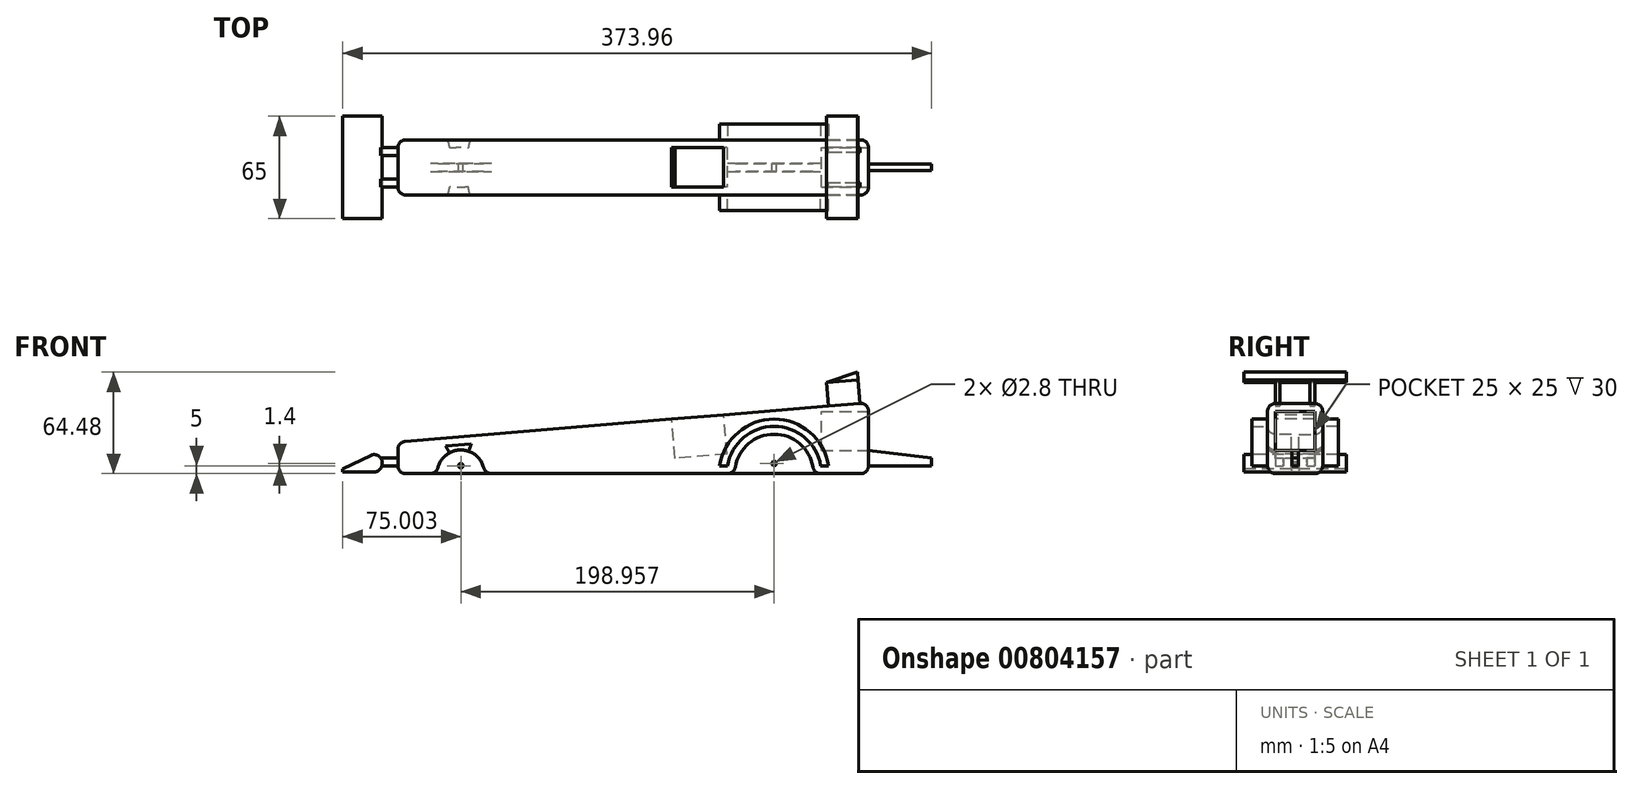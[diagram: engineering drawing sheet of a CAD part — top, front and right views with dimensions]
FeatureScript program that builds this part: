
annotation { "Feature Type Name" : "Feature", "Feature Type Description" : "" }
export const myFeature = defineFeature(function(context is Context, id is Id, definition is map)
    precondition{}
    {
        {
            var Q0;
            Q0=qCreatedBy(makeId("Front.planeOp"),FACE);
            var sketch = newSketch(context, id + "F0", { "sketchPlane" : qUnion([Q0])});
            skLineSegment(sketch, "E0", {"start": v(0, 0) * mm, "end": v(-298.96, -25) * mm});
            skLineSegment(sketch, "E1", {"start": v(-298.96, -25) * mm, "end": v(-298.96, -45) * mm});
            skLineSegment(sketch, "E2", {"start": v(-298.96, -45) * mm, "end": v(0, -45) * mm});
            skLineSegment(sketch, "E3", {"start": v(0, -45) * mm, "end": v(0, 0) * mm});
            skSolve(sketch);
        }
        {
            var Q0;
            Q0 = qSketchRegion(id + "F0", true);
            extrude(context, id + "F1", {"entities" : qUnion([Q0]), "depth" : 35 * mm, "offsetDistance" : 25 * mm});
        }
        {
            var Q0;
            Q0=makeQuery(id+"F1.opExtrude","CAP_FACE",FACE,{"disambiguationData":[OSD([sQuery(id+"F0.wireOp",EDGE,"E0"),sQuery(id+"F0.wireOp",EDGE,"E1"),sQuery(id+"F0.wireOp",EDGE,"E2"),sQuery(id+"F0.wireOp",EDGE,"E3")])],"isStart":false});
            var sketch = newSketch(context, id + "F2", { "sketchPlane" : qUnion([Q0])});
            skCircle(sketch, "E4", {"center": v(-258.96, -45) * mm, "radius": 15 * mm});
            skSolve(sketch);
        }
        {
            var Q0;
            Q0 = qSketchRegion(id + "F2", true);
            var Q1;
            Q1=makeQuery(id+"F1.opExtrude","CAP_FACE",FACE,{"disambiguationData":[OSD([sQuery(id+"F0.wireOp",EDGE,"E0"),sQuery(id+"F0.wireOp",EDGE,"E1"),sQuery(id+"F0.wireOp",EDGE,"E2"),sQuery(id+"F0.wireOp",EDGE,"E3")])],"isStart":true});
            extrude(context, id + "F3", {"entities" : qUnion([Q0, Q1]), "operationType" : NewBodyOperationType.REMOVE, "oppositeDirection" : true, "depth" : 15 * mm, "offsetDistance" : 25 * mm});
        }
        {
            var Q0;
            Q0=makeQuery(id+"F1.opExtrude","CAP_FACE",FACE,{"disambiguationData":[OSD([sQuery(id+"F0.wireOp",EDGE,"E0"),sQuery(id+"F0.wireOp",EDGE,"E1"),sQuery(id+"F0.wireOp",EDGE,"E2"),sQuery(id+"F0.wireOp",EDGE,"E3")])],"isStart":true});
            var sketch = newSketch(context, id + "F4", { "sketchPlane" : qUnion([Q0])});
            skCircle(sketch, "E5", {"center": v(258.96, -45) * mm, "radius": 15 * mm});
            skSolve(sketch);
        }
        {
            var Q0;
            Q0 = qSketchRegion(id + "F4", true);
            extrude(context, id + "F5", {"entities" : qUnion([Q0]), "operationType" : NewBodyOperationType.REMOVE, "oppositeDirection" : true, "depth" : 15 * mm, "offsetDistance" : 25 * mm});
        }
        {
            var Q0;
            Q0=makeQuery(id+"F5.boolean.opBoolean","COPY",FACE,{"derivedFrom":makeQuery(id+"F5.opExtrude","CAP_FACE",FACE,{"disambiguationData":[OSD([sQuery(id+"F4.wireOp",EDGE,"E5")])],"isStart":false})});
            var sketch = newSketch(context, id + "F6", { "sketchPlane" : qUnion([Q0])});
            skCircle(sketch, "E6", {"center": v(258.96, -40) * mm, "radius": 1.4 * mm});
            skPoint(sketch, "E6.centerSnap0", {"position": v(258.96, -45) * mm});
            skSolve(sketch);
        }
        {
            var Q0;
            Q0 = qSketchRegion(id + "F6", true);
            extrude(context, id + "F7", {"entities" : qUnion([Q0]), "operationType" : NewBodyOperationType.REMOVE, "oppositeDirection" : true, "depth" : 25 * mm, "offsetDistance" : 25 * mm});
        }
        {
            var Q0;
            Q0=makeQuery(id+"F1.opExtrude","CAP_FACE",FACE,{"disambiguationData":[OSD([sQuery(id+"F0.wireOp",EDGE,"E0"),sQuery(id+"F0.wireOp",EDGE,"E1"),sQuery(id+"F0.wireOp",EDGE,"E2"),sQuery(id+"F0.wireOp",EDGE,"E3")])],"isStart":false});
            var sketch = newSketch(context, id + "F8", { "sketchPlane" : qUnion([Q0])});
            skCircle(sketch, "E7", {"center": v(-60, -45) * mm, "radius": 25 * mm});
            skSolve(sketch);
        }
        {
            var Q0;
            Q0 = qSketchRegion(id + "F8", true);
            extrude(context, id + "F9", {"entities" : qUnion([Q0]), "operationType" : NewBodyOperationType.REMOVE, "oppositeDirection" : true, "depth" : 15 * mm, "offsetDistance" : 25 * mm});
        }
        {
            var Q0;
            Q0=makeQuery(id+"F1.opExtrude","CAP_FACE",FACE,{"disambiguationData":[OSD([sQuery(id+"F0.wireOp",EDGE,"E0"),sQuery(id+"F0.wireOp",EDGE,"E1"),sQuery(id+"F0.wireOp",EDGE,"E2"),sQuery(id+"F0.wireOp",EDGE,"E3")])],"isStart":true});
            var sketch = newSketch(context, id + "F10", { "sketchPlane" : qUnion([Q0])});
            skCircle(sketch, "E8", {"center": v(60, -45) * mm, "radius": 25 * mm});
            skSolve(sketch);
        }
        {
            var Q0;
            Q0 = qSketchRegion(id + "F10", true);
            extrude(context, id + "F11", {"entities" : qUnion([Q0]), "operationType" : NewBodyOperationType.REMOVE, "oppositeDirection" : true, "depth" : 15 * mm, "offsetDistance" : 25 * mm});
        }
        {
            var Q0;
            Q0=makeQuery(id+"F11.boolean.opBoolean","COPY",FACE,{"derivedFrom":makeQuery(id+"F11.opExtrude","CAP_FACE",FACE,{"disambiguationData":[OSD([sQuery(id+"F10.wireOp",EDGE,"E8")])],"isStart":false})});
            var sketch = newSketch(context, id + "F12", { "sketchPlane" : qUnion([Q0])});
            skCircle(sketch, "E9", {"center": v(60, -38.6) * mm, "radius": 1.4 * mm});
            skPoint(sketch, "E9.centerSnap0", {"position": v(60, -45) * mm});
            skSolve(sketch);
        }
        {
            var Q0;
            Q0=makeQuery(id+"F12.imprint","IMPRINT",FACE,{"disambiguationData":[TD([[makeQuery(id+"F12.imprint","IMPRINT",EDGE,{"derivedFrom":sQuery(id+"F12.wireOp",EDGE,"E9")}),1.0]])]});
            extrude(context, id + "F13", {"entities" : qUnion([Q0]), "operationType" : NewBodyOperationType.REMOVE, "oppositeDirection" : true, "depth" : 25 * mm, "offsetDistance" : 25 * mm});
        }
        {
            var Q0;
            Q0=makeQuery(id+"F1.opExtrude","CAP_EDGE",EDGE,{"disambiguationData":[OSD([sQuery(id+"F0.wireOp",EDGE,"E0")])],"isStart":true});
            fillet(context, id + "F14", {"entities" : qUnion([Q0]), "radius" : 5 * mm, "tangentPropagation" : true, "allowEdgeOverflow" : false});
        }
        {
            var Q0;
            Q0=makeQuery(id+"F1.opExtrude","CAP_EDGE",EDGE,{"disambiguationData":[OSD([sQuery(id+"F0.wireOp",EDGE,"E0")])],"isStart":false});
            fillet(context, id + "F15", {"entities" : qUnion([Q0]), "radius" : 5 * mm, "tangentPropagation" : true, "allowEdgeOverflow" : false});
        }
        {
            var Q0;
            Q0=makeQuery(id+"F1.opExtrude","SWEPT_EDGE",EDGE,{"disambiguationData":[OSD([sQuery(id+"F0.wireOp",EDGE,"E0"),sQuery(id+"F0.wireOp",EDGE,"E1")])]});
            fillet(context, id + "F16", {"entities" : qUnion([Q0]), "radius" : 5 * mm, "tangentPropagation" : true, "allowEdgeOverflow" : false});
        }
        {
            var Q0;
            Q0=makeQuery(id+"F1.opExtrude","SWEPT_EDGE",EDGE,{"disambiguationData":[OSD([sQuery(id+"F0.wireOp",EDGE,"E0"),sQuery(id+"F0.wireOp",EDGE,"E3")])]});
            fillet(context, id + "F17", {"entities" : qUnion([Q0]), "radius" : 5 * mm, "tangentPropagation" : true, "allowEdgeOverflow" : false});
        }
        {
            var Q0;
            {var subQ0=sQuery(id+"F0.wireOp",EDGE,"E3");var subQ1=sQuery(id+"F0.wireOp",EDGE,"E2");var subQ4=makeQuery(id+"F3.opExtrude","SWEPT_FACE",FACE,{"disambiguationData":[OSD([sQuery(id+"F2.wireOp",EDGE,"E4")])]});Q0=makeQuery(id+"F9.boolean.opBoolean","SPLIT",EDGE,{"disambiguationData":[TD([makeQuery(id+"F3.boolean.opBoolean","COPY",FACE,{"derivedFrom":subQ4})])],"derivedFrom":makeQuery(id+"F3.boolean.opBoolean","SPLIT",EDGE,{"disambiguationData":[TD([makeQuery(id+"F1.opExtrude","SWEPT_FACE",FACE,{"disambiguationData":[OSD([subQ0])]})])],"derivedFrom":makeQuery(id+"F1.opExtrude","CAP_EDGE",EDGE,{"disambiguationData":[OSD([subQ1])],"isStart":false})})});}
            var Q1;
            Q1=makeQuery(id+"F1.opExtrude","CAP_FACE",FACE,{"disambiguationData":[OSD([sQuery(id+"F0.wireOp",EDGE,"E0"),sQuery(id+"F0.wireOp",EDGE,"E1"),sQuery(id+"F0.wireOp",EDGE,"E2"),sQuery(id+"F0.wireOp",EDGE,"E3")])],"isStart":false});
            fillet(context, id + "F18", {"entities" : qUnion([Q0, Q1]), "radius" : 5 * mm, "tangentPropagation" : true, "allowEdgeOverflow" : false});
        }
        {
            var Q0;
            Q0=makeQuery(id+"F1.opExtrude","CAP_FACE",FACE,{"disambiguationData":[OSD([sQuery(id+"F0.wireOp",EDGE,"E0"),sQuery(id+"F0.wireOp",EDGE,"E1"),sQuery(id+"F0.wireOp",EDGE,"E2"),sQuery(id+"F0.wireOp",EDGE,"E3")])],"isStart":true});
            fillet(context, id + "F19", {"entities" : qUnion([Q0]), "radius" : 5 * mm, "tangentPropagation" : true, "allowEdgeOverflow" : false});
        }
        {
            var Q0;
            Q0=makeQuery(id+"F1.opExtrude","SWEPT_FACE",FACE,{"disambiguationData":[OSD([sQuery(id+"F0.wireOp",EDGE,"E0")])]});
            var sketch = newSketch(context, id + "F20", { "sketchPlane" : qUnion([Q0])});
            skLineSegment(sketch, "E10", {"start": v(-5.44, -5) * mm, "end": v(-25.44, -5) * mm});
            skLineSegment(sketch, "E11", {"start": v(-5.44, -30) * mm, "end": v(-25.44, -30) * mm});
            skLineSegment(sketch, "E12", {"start": v(-5.44, -5) * mm, "end": v(-5.44, -8) * mm});
            skLineSegment(sketch, "E13", {"start": v(-5.44, -8) * mm, "end": v(-25.44, -8) * mm});
            skLineSegment(sketch, "E14", {"start": v(-25.44, -8) * mm, "end": v(-25.44, -5) * mm});
            skLineSegment(sketch, "E15", {"start": v(-25.44, -30) * mm, "end": v(-25.44, -27) * mm});
            skLineSegment(sketch, "E16", {"start": v(-25.44, -27) * mm, "end": v(-5.44, -27) * mm});
            skLineSegment(sketch, "E17", {"start": v(-5.44, -27) * mm, "end": v(-5.44, -30) * mm});
            skSolve(sketch);
        }
        {
            var Q0;
            Q0 = qSketchRegion(id + "F20", true);
            extrude(context, id + "F21", {"entities" : qUnion([Q0]), "operationType" : NewBodyOperationType.ADD, "depth" : 15 * mm, "offsetDistance" : 25 * mm});
        }
        {
            var Q0;
            Q0=makeQuery(id+"F21.opExtrude","CAP_FACE",FACE,{"disambiguationData":[OSD([sQuery(id+"F20.wireOp",EDGE,"E10"),sQuery(id+"F20.wireOp",EDGE,"E12"),sQuery(id+"F20.wireOp",EDGE,"E13"),sQuery(id+"F20.wireOp",EDGE,"E14")])],"isStart":false});
            var sketch = newSketch(context, id + "F22", { "sketchPlane" : qUnion([Q0])});
            skLineSegment(sketch, "E18", {"start": v(-25.44, -5) * mm, "end": v(-25.44, -29.95) * mm});
            skLineSegment(sketch, "E19", {"start": v(-5.53, -29.95) * mm, "end": v(-5.44, -5) * mm});
            skLineSegment(sketch, "E20", {"start": v(-25.44, -5) * mm, "end": v(-25.44, 15) * mm});
            skLineSegment(sketch, "E21", {"start": v(-25.44, 15) * mm, "end": v(-5.44, 15) * mm});
            skLineSegment(sketch, "E22", {"start": v(-5.44, 15) * mm, "end": v(-5.44, -5) * mm});
            skLineSegment(sketch, "E23", {"start": v(-25.44, -29.95) * mm, "end": v(-25.44, -49.95) * mm});
            skLineSegment(sketch, "E24", {"start": v(-25.44, -49.95) * mm, "end": v(-5.53, -49.95) * mm});
            skLineSegment(sketch, "E25", {"start": v(-5.53, -49.95) * mm, "end": v(-5.53, -29.95) * mm});
            skSolve(sketch);
        }
        {
            var Q0;
            Q0 = qSketchRegion(id + "F22", true);
            extrude(context, id + "F23", {"entities" : qUnion([Q0]), "operationType" : NewBodyOperationType.ADD, "depth" : 5 * mm, "offsetDistance" : 25 * mm});
        }
        {
            var Q0;
            Q0=makeQuery(id+"F23.opExtrude","SWEPT_FACE",FACE,{"disambiguationData":[OSD([sQuery(id+"F22.wireOp",EDGE,"E24")])]});
            var sketch = newSketch(context, id + "F24", { "sketchPlane" : qUnion([Q0])});
            skLineSegment(sketch, "E26", {"start": v(-26.6, 12.83) * mm, "end": v(-7.18, 19.47) * mm});
            skSolve(sketch);
        }
        {
            var Q0;
            Q0 = qSketchRegion(id + "F24", true);
            var Q1;
            Q1=makeQuery(id+"F24.imprint","IMPRINT",FACE,{"disambiguationData":[TD([[makeQuery(id+"F24.imprint","IMPRINT",EDGE,{"derivedFrom":sQuery(id+"F24.wireOp",EDGE,"E26")}),1.0]])]});
            extrude(context, id + "F25", {"entities" : qUnion([Q0, Q1]), "operationType" : NewBodyOperationType.REMOVE, "oppositeDirection" : true, "depth" : 100 * mm, "offsetDistance" : 25 * mm});
        }
        {
            var Q0;
            Q0=makeQuery(id+"F1.opExtrude","SWEPT_FACE",FACE,{"disambiguationData":[OSD([sQuery(id+"F0.wireOp",EDGE,"E1")])]});
            var sketch = newSketch(context, id + "F26", { "sketchPlane" : qUnion([Q0])});
            skLineSegment(sketch, "E27", {"start": v(5, -35) * mm, "end": v(10, -35) * mm});
            skLineSegment(sketch, "E28", {"start": v(10, -35) * mm, "end": v(10, -40) * mm});
            skLineSegment(sketch, "E29", {"start": v(10, -40) * mm, "end": v(5, -40) * mm});
            skLineSegment(sketch, "E30", {"start": v(5, -40) * mm, "end": v(5, -35) * mm});
            skLineSegment(sketch, "E31", {"start": v(30, -35) * mm, "end": v(25, -35) * mm});
            skPoint(sketch, "E31.startSnap0", {"position": v(30, -34.8) * mm});
            skLineSegment(sketch, "E32", {"start": v(25, -35) * mm, "end": v(25, -40) * mm});
            skLineSegment(sketch, "E33", {"start": v(25, -40) * mm, "end": v(30, -40) * mm});
            skLineSegment(sketch, "E34", {"start": v(30, -40) * mm, "end": v(30, -34.8) * mm});
            skSolve(sketch);
        }
        {
            var Q0;
            Q0 = qSketchRegion(id + "F26", true);
            extrude(context, id + "F27", {"entities" : qUnion([Q0]), "operationType" : NewBodyOperationType.ADD, "depth" : 10 * mm, "offsetDistance" : 25 * mm});
        }
        {
            var Q0;
            Q0=makeQuery(id+"F27.opExtrude","CAP_FACE",FACE,{"disambiguationData":[OSD([sQuery(id+"F26.wireOp",EDGE,"E27"),sQuery(id+"F26.wireOp",EDGE,"E28"),sQuery(id+"F26.wireOp",EDGE,"E29"),sQuery(id+"F26.wireOp",EDGE,"E30")])],"isStart":false});
            var sketch = newSketch(context, id + "F28", { "sketchPlane" : qUnion([Q0])});
            skLineSegment(sketch, "E35", {"start": v(5, -30) * mm, "end": v(30, -30) * mm});
            skLineSegment(sketch, "E36", {"start": v(5, -44) * mm, "end": v(30, -44) * mm});
            skLineSegment(sketch, "E37", {"start": v(5, -30) * mm, "end": v(-15, -30) * mm});
            skLineSegment(sketch, "E38", {"start": v(-15, -30) * mm, "end": v(-15, -44) * mm});
            skLineSegment(sketch, "E39", {"start": v(-15, -44) * mm, "end": v(5, -44) * mm});
            skLineSegment(sketch, "E40", {"start": v(30, -30) * mm, "end": v(50, -30) * mm});
            skLineSegment(sketch, "E41", {"start": v(50, -30) * mm, "end": v(50, -44) * mm});
            skLineSegment(sketch, "E42", {"start": v(50, -44) * mm, "end": v(30, -44) * mm});
            skPoint(sketch, "E43.end.orphan", {"position": v(30, -40) * mm});
            skSolve(sketch);
        }
        {
            var Q0;
            Q0 = qSketchRegion(id + "F28", true);
            extrude(context, id + "F29", {"entities" : qUnion([Q0]), "operationType" : NewBodyOperationType.ADD, "depth" : 25 * mm, "offsetDistance" : 25 * mm});
        }
        {
            var Q0;
            Q0=makeQuery(id+"F29.opExtrude","SWEPT_FACE",FACE,{"disambiguationData":[OSD([sQuery(id+"F28.wireOp",EDGE,"E41")])]});
            var sketch = newSketch(context, id + "F30", { "sketchPlane" : qUnion([Q0])});
            skPoint(sketch, "E44.start.orphan", {"position": v(-347.74, -13.28) * mm});
            skLineSegment(sketch, "E45", {"start": v(-333.96, -42) * mm, "end": v(-308.96, -30) * mm});
            skSolve(sketch);
        }
        {
            var Q0;
            Q0 = qSketchRegion(id + "F30", true);
            var Q1;
            {var subQ0=sQuery(id+"F30.wireOp",EDGE,"E44");Q1=makeQuery(id+"F30.imprint","IMPRINT",FACE,{"disambiguationData":[TD([[makeQuery(id+"F30.imprint","IMPRINT",EDGE,{"derivedFrom":subQ0}),1.0]])]});}
            var Q2;
            {var subQ0=sQuery(id+"F30.wireOp",EDGE,"E45");Q2=makeQuery(id+"F30.imprint","IMPRINT",FACE,{"disambiguationData":[TD([[makeQuery(id+"F30.imprint","IMPRINT",EDGE,{"derivedFrom":subQ0}),1.0]])]});}
            extrude(context, id + "F31", {"entities" : qUnion([Q0, Q1, Q2]), "operationType" : NewBodyOperationType.REMOVE, "oppositeDirection" : true, "depth" : 100 * mm, "offsetDistance" : 25 * mm});
        }
        {
            var Q0;
            Q0=makeQuery(id+"F1.opExtrude","SWEPT_FACE",FACE,{"disambiguationData":[OSD([sQuery(id+"F0.wireOp",EDGE,"E0")])]});
            var sketch = newSketch(context, id + "F32", { "sketchPlane" : qUnion([Q0])});
            skLineSegment(sketch, "E46", {"start": v(-92.33, -5) * mm, "end": v(-92.33, -30) * mm});
            skLineSegment(sketch, "E47", {"start": v(-125.47, -5) * mm, "end": v(-125.47, -30) * mm});
            skSolve(sketch);
        }
        {
            var Q0;
            Q0 = qSketchRegion(id + "F32", true);
            var Q1;
            {var subQ0=sQuery(id+"F32.wireOp",EDGE,"E46");Q1=makeQuery(id+"F32.imprint","IMPRINT",FACE,{"disambiguationData":[TD([[makeQuery(id+"F32.imprint","IMPRINT",EDGE,{"derivedFrom":subQ0}),-1.0]])]});}
            extrude(context, id + "F33", {"entities" : qUnion([Q0, Q1]), "operationType" : NewBodyOperationType.REMOVE, "oppositeDirection" : true, "depth" : 25 * mm, "offsetDistance" : 25 * mm});
        }
        {
            var Q0;
            Q0=makeQuery(id+"F1.opExtrude","SWEPT_FACE",FACE,{"disambiguationData":[OSD([sQuery(id+"F0.wireOp",EDGE,"E3")])]});
            var sketch = newSketch(context, id + "F34", { "sketchPlane" : qUnion([Q0])});
            skLineSegment(sketch, "E48", {"start": v(-30, -5.44) * mm, "end": v(-30, -30.44) * mm});
            skLineSegment(sketch, "E49", {"start": v(-30, -30.44) * mm, "end": v(-5, -30.44) * mm});
            skLineSegment(sketch, "E50", {"start": v(-5, -30.44) * mm, "end": v(-5, -5.44) * mm});
            skLineSegment(sketch, "E51", {"start": v(-5, -5.44) * mm, "end": v(-30, -5.44) * mm});
            skSolve(sketch);
        }
        {
            var Q0;
            Q0 = qSketchRegion(id + "F34", true);
            var Q1;
            Q1=makeQuery(id+"F34.imprint","IMPRINT",FACE,{"disambiguationData":[TD([[makeQuery(id+"F34.imprint","IMPRINT",EDGE,{"derivedFrom":sQuery(id+"F34.wireOp",EDGE,"E48")}),1.0]])]});
            extrude(context, id + "F35", {"entities" : qUnion([Q0, Q1]), "operationType" : NewBodyOperationType.REMOVE, "oppositeDirection" : true, "depth" : 30 * mm, "offsetDistance" : 25 * mm});
        }
        {
            var Q0;
            Q0=makeQuery(id+"F9.boolean.opBoolean","INTERSECT",EDGE,{"disambiguationData":[OD(0.0)],"derivedFrom":[makeQuery(id+"F1.opExtrude","SWEPT_FACE",FACE,{"disambiguationData":[OSD([sQuery(id+"F0.wireOp",EDGE,"E2")])]}),makeQuery(id+"F9.opExtrude","SWEPT_FACE",FACE,{"disambiguationData":[OSD([sQuery(id+"F8.wireOp",EDGE,"E7")])]})]});
            var Q1;
            Q1=makeQuery(id+"F3.boolean.opBoolean","INTERSECT",EDGE,{"disambiguationData":[OD(0.0)],"derivedFrom":[makeQuery(id+"F1.opExtrude","SWEPT_FACE",FACE,{"disambiguationData":[OSD([sQuery(id+"F0.wireOp",EDGE,"E2")])]}),makeQuery(id+"F3.opExtrude","SWEPT_FACE",FACE,{"disambiguationData":[OSD([sQuery(id+"F2.wireOp",EDGE,"E4")])]})]});
            var Q2;
            Q2=makeQuery(id+"F3.boolean.opBoolean","INTERSECT",EDGE,{"disambiguationData":[OD(1.0)],"derivedFrom":[makeQuery(id+"F1.opExtrude","SWEPT_FACE",FACE,{"disambiguationData":[OSD([sQuery(id+"F0.wireOp",EDGE,"E2")])]}),makeQuery(id+"F3.opExtrude","SWEPT_FACE",FACE,{"disambiguationData":[OSD([sQuery(id+"F2.wireOp",EDGE,"E4")])]})]});
            var Q3;
            Q3=makeQuery(id+"F5.boolean.opBoolean","INTERSECT",EDGE,{"disambiguationData":[OD(1.0)],"derivedFrom":[makeQuery(id+"F1.opExtrude","SWEPT_FACE",FACE,{"disambiguationData":[OSD([sQuery(id+"F0.wireOp",EDGE,"E2")])]}),makeQuery(id+"F5.opExtrude","SWEPT_FACE",FACE,{"disambiguationData":[OSD([sQuery(id+"F4.wireOp",EDGE,"E5")])]})]});
            var Q4;
            Q4=makeQuery(id+"F11.boolean.opBoolean","INTERSECT",EDGE,{"disambiguationData":[OD(1.0)],"derivedFrom":[makeQuery(id+"F1.opExtrude","SWEPT_FACE",FACE,{"disambiguationData":[OSD([sQuery(id+"F0.wireOp",EDGE,"E2")])]}),makeQuery(id+"F11.opExtrude","SWEPT_FACE",FACE,{"disambiguationData":[OSD([sQuery(id+"F10.wireOp",EDGE,"E8")])]})]});
            var Q5;
            Q5=makeQuery(id+"F9.boolean.opBoolean","INTERSECT",EDGE,{"disambiguationData":[OD(1.0)],"derivedFrom":[makeQuery(id+"F1.opExtrude","SWEPT_FACE",FACE,{"disambiguationData":[OSD([sQuery(id+"F0.wireOp",EDGE,"E2")])]}),makeQuery(id+"F9.opExtrude","SWEPT_FACE",FACE,{"disambiguationData":[OSD([sQuery(id+"F8.wireOp",EDGE,"E7")])]})]});
            fillet(context, id + "F36", {"entities" : qUnion([Q0, Q1, Q2, Q3, Q4, Q5]), "radius" : 5 * mm, "tangentPropagation" : true, "allowEdgeOverflow" : false});
        }
        {
            var Q0;
            {var subQ0=sQuery(id+"F28.wireOp",EDGE,"E40");Q0=makeQuery(id+"F31.boolean.opBoolean","MERGE",EDGE,{"derivedFrom":[makeQuery(id+"F29.opExtrude","CAP_EDGE",EDGE,{"disambiguationData":[OSD([sQuery(id+"F28.wireOp",EDGE,"E35"),sQuery(id+"F28.wireOp",EDGE,"E37"),subQ0])],"isStart":true}),makeQuery(id+"F31.opExtrude","SWEPT_EDGE",EDGE,{"disambiguationData":[OSD([subQ0,sQuery(id+"F28.wireOp",EDGE,"E41"),sQuery(id+"F30.wireOp",EDGE,"E45")])]})]});}
            var Q1;
            Q1=makeQuery(id+"F31.boolean.opBoolean","COPY",EDGE,{"derivedFrom":makeQuery(id+"F31.opExtrude","SWEPT_EDGE",EDGE,{"disambiguationData":[OSD([sQuery(id+"F28.wireOp",EDGE,"E41"),sQuery(id+"F30.wireOp",EDGE,"E45")])]})});
            fillet(context, id + "F37", {"entities" : qUnion([Q0, Q1]), "radius" : 5 * mm, "tangentPropagation" : true, "allowEdgeOverflow" : false});
        }
        {
            var Q0;
            Q0=makeQuery(id+"F29.opExtrude","CAP_EDGE",EDGE,{"disambiguationData":[OSD([sQuery(id+"F28.wireOp",EDGE,"E36"),sQuery(id+"F28.wireOp",EDGE,"E39"),sQuery(id+"F28.wireOp",EDGE,"E42")])],"isStart":true});
            fillet(context, id + "F38", {"entities" : qUnion([Q0]), "radius" : 5 * mm, "tangentPropagation" : true, "allowEdgeOverflow" : false});
        }
        {
            var Q0;
            Q0=makeQuery(id+"F18.opFillet","SPLIT",FACE,{"disambiguationData":[OD(0.0)],"derivedFrom":makeQuery(id+"F1.opExtrude","CAP_FACE",FACE,{"disambiguationData":[OSD([sQuery(id+"F0.wireOp",EDGE,"E0"),sQuery(id+"F0.wireOp",EDGE,"E1"),sQuery(id+"F0.wireOp",EDGE,"E2"),sQuery(id+"F0.wireOp",EDGE,"E3")])],"isStart":false})});
            var sketch = newSketch(context, id + "F39", { "sketchPlane" : qUnion([Q0])});
            skArc(sketch, "E52", {"start": v(-25.42, -40) * mm, "mid": v(-60, -10.4) * mm, "end": v(-94.58, -40) * mm});
            skSolve(sketch);
        }
        {
            var Q0;
            Q0 = qSketchRegion(id + "F39", true);
            var Q1;
            {var subQ0=sQuery(id+"F39.wireOp",EDGE,"E52");Q1=makeQuery(id+"F39.imprint","IMPRINT",FACE,{"disambiguationData":[TD([[makeQuery(id+"F39.imprint","IMPRINT",EDGE,{"derivedFrom":subQ0}),1.0]])]});}
            extrude(context, id + "F40", {"entities" : qUnion([Q0, Q1]), "operationType" : NewBodyOperationType.ADD, "depth" : 10 * mm, "offsetDistance" : 25 * mm});
        }
        {
            var Q0;
            Q0=makeQuery(id+"F19.opFillet","SPLIT",FACE,{"disambiguationData":[OD(1.0)],"derivedFrom":makeQuery(id+"F1.opExtrude","CAP_FACE",FACE,{"disambiguationData":[OSD([sQuery(id+"F0.wireOp",EDGE,"E0"),sQuery(id+"F0.wireOp",EDGE,"E1"),sQuery(id+"F0.wireOp",EDGE,"E2"),sQuery(id+"F0.wireOp",EDGE,"E3")])],"isStart":true})});
            var sketch = newSketch(context, id + "F41", { "sketchPlane" : qUnion([Q0])});
            skArc(sketch, "E53", {"start": v(94.58, -40) * mm, "mid": v(60, -10.4) * mm, "end": v(25.42, -40) * mm});
            skSolve(sketch);
        }
        {
            var Q0;
            Q0 = qSketchRegion(id + "F41", true);
            var Q1;
            {var subQ0=sQuery(id+"F41.wireOp",EDGE,"E53");Q1=makeQuery(id+"F41.imprint","IMPRINT",FACE,{"disambiguationData":[TD([[makeQuery(id+"F41.imprint","IMPRINT",EDGE,{"derivedFrom":subQ0}),1.0]])]});}
            extrude(context, id + "F42", {"entities" : qUnion([Q0, Q1]), "operationType" : NewBodyOperationType.ADD, "depth" : 10 * mm, "offsetDistance" : 25 * mm});
        }
        {
            var Q0;
            Q0=makeQuery(id+"F1.opExtrude","SWEPT_FACE",FACE,{"disambiguationData":[OSD([sQuery(id+"F0.wireOp",EDGE,"E3")])]});
            var sketch = newSketch(context, id + "F43", { "sketchPlane" : qUnion([Q0])});
            skLineSegment(sketch, "E54", {"start": v(-19.5, -30.44) * mm, "end": v(-19.5, -40) * mm});
            skLineSegment(sketch, "E55", {"start": v(-15.5, -30.44) * mm, "end": v(-15.5, -40) * mm});
            skLineSegment(sketch, "E56", {"start": v(-19.5, -30.44) * mm, "end": v(-15.5, -30.44) * mm});
            skLineSegment(sketch, "E57", {"start": v(-19.5, -40) * mm, "end": v(-15.5, -40) * mm});
            skPoint(sketch, "E58.end.orphan", {"position": v(-17.5, -30.44) * mm});
            skPoint(sketch, "E58.start.orphan", {"position": v(-17.5, -40) * mm});
            skSolve(sketch);
        }
        {
            var Q0;
            Q0 = qSketchRegion(id + "F43", true);
            extrude(context, id + "F44", {"entities" : qUnion([Q0]), "operationType" : NewBodyOperationType.ADD, "depth" : 40 * mm, "offsetDistance" : 25 * mm});
        }
        {
            var Q0;
            Q0=makeQuery(id+"F44.opExtrude","SWEPT_FACE",FACE,{"disambiguationData":[OSD([sQuery(id+"F43.wireOp",EDGE,"E55")])]});
            var sketch = newSketch(context, id + "F45", { "sketchPlane" : qUnion([Q0])});
            skLineSegment(sketch, "E59", {"start": v(-40, -35.22) * mm, "end": v(0, -30.44) * mm});
            skSolve(sketch);
        }
        {
            var Q0;
            Q0 = qSketchRegion(id + "F45", true);
            var Q1;
            {var subQ0=sQuery(id+"F45.wireOp",EDGE,"E59");Q1=makeQuery(id+"F45.imprint","IMPRINT",FACE,{"disambiguationData":[TD([[makeQuery(id+"F45.imprint","IMPRINT",EDGE,{"derivedFrom":subQ0}),1.0]])]});}
            extrude(context, id + "F46", {"entities" : qUnion([Q0, Q1]), "operationType" : NewBodyOperationType.REMOVE, "oppositeDirection" : true, "depth" : 25 * mm, "offsetDistance" : 25 * mm});
        }
    });
